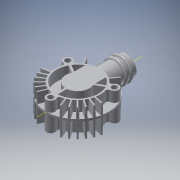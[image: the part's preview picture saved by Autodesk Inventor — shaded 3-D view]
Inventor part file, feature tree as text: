
AUTODESK INVENTOR PART (.ipt)
format: ipt  version: 2016 (Build 200138000, 138)  size: 2,456,576 bytes
history: native  units: in
note: dims shown in document units (in); Inventor stores cm internally (conversion verified against a paired STEP export)
features: sketch x24, extrude x21, pattern_circular x9, plane x4, draft x4, mirror x3, fillet x2, hole x2, revolve x2, other x1, thread x1
ambient origin geometry x8: Origin, YZ Plane, XZ Plane, XY Plane, X Axis, Y Axis, Z Axis, Center Point
bodies: Solid1 (feature_tree)
feature tree (73):
  extrude  "Extrusion1"  Depth=0.05in TaperAngle=0.0deg
  extrude  "Extrusion2"  Depth=1.08in
  extrude  "Extrusion3"  Depth=0.5in
  pattern_circular  "Circular Pattern1"  Count=3 Angle=360.0deg
  plane  "Work Plane2"
  extrude  "Extrusion17"  Depth=0.25in TaperAngle=0.0deg
  extrude  "Extrusion20"  Depth=0.25in
  draft  "FaceDraft5"
  draft  "FaceDraft6"
  fillet  "Fillet6"  Radius=0.125in
  pattern_circular  "Circular Pattern7"  Count=3 Angle=360.0deg
  extrude  "Extrusion21"  Depth=0.25in TaperAngle=360.0deg
  pattern_circular  "Circular Pattern8"  [2 undecoded]
  extrude  "Extrusion22"  Depth=0.25in
  draft  "FaceDraft7"
  draft  "FaceDraft8"
  fillet  "Fillet7"  Radius=0.125in
  pattern_circular  "Circular Pattern9"  [2 undecoded]
  extrude  "Extrusion23"  Depth=0.25in
  pattern_circular  "Circular Pattern10"  [2 undecoded]
  hole  "Hole1"  [1 undecoded]
  pattern_circular  "Circular Pattern11"  [2 undecoded]
  extrude  "Extrusion24"  Depth=0.25in
  plane  "Work Plane5"
  extrude  "Extrusion25"  Depth=0.25in TaperAngle=0.0deg
  hole  "Hole2"  [1 undecoded]
  other  "Work Axis1"
  revolve  "Revolution2"  [1 undecoded]
  pattern_circular  "Circular Pattern2"  [2 undecoded]
  extrude  "Extrusion5"  Depth=0.25in TaperAngle=360.0deg
  extrude  "Extrusion6"  Depth=0.25in
  mirror  "Mirror1"
  mirror  "Mirror2"
  extrude  "Extrusion7"  Depth=0.25in
  extrude  "Extrusion8"  Depth=0.25in TaperAngle=0.0deg
  extrude  "Extrusion9"  Depth=0.25in TaperAngle=360.0deg
  pattern_circular  "Circular Pattern3"  [2 undecoded]
  mirror  "Mirror3"
  extrude  "Extrusion10"  Depth=0.25in
  pattern_circular  "Circular Pattern4"  [2 undecoded]
  extrude  "Extrusion11"  Depth=0.25in
  plane  "Work Plane1"
  extrude  "Extrusion12"  Depth=0.25in TaperAngle=360.0deg
  extrude  "Extrusion13"  Depth=0.25in TaperAngle=0.0deg
  revolve  "Revolution1"  Angle=360.0deg
  extrude  "Extrusion14"  Depth=0.25in
  extrude  "Extrusion16"  Depth=0.25in TaperAngle=360.0deg
  thread  "Thread1"  [1 undecoded]
  sketch  "Sketch1"  dims[d0=1.5in d1=0.05in d2=0.0in]
  sketch  "Sketch2"  dims[d3=1.0in d4=1.08in]
  sketch  "Sketch3"  dims[d5=0.5625in d6=0.5in]
  sketch  "Sketch5"  dims[d7=0.25in d8=0.0in]
  sketch  "Sketch6"  dims[d9=0.05in]
  sketch  "Sketch7"  dims[d10=0.25in d11=0.0in d12=1.1811in d13=360.0deg]
  sketch  "Sketch8"  dims[d20=11.0236in d21=360.0deg d23=0.25in d24=0.0in]
  sketch  "Sketch9"  dims[d25=0.25in d26=0.0in d27=0.5in d28=0.125in d29=0.0in]
  sketch  "Sketch10"  dims[d30=1.0in]
  sketch  "Sketch11"  dims[d31=0.25in d32=0.0in]
  sketch  "Sketch12"  dims[d35=0.25in]
  sketch  "Sketch13"  dims[d36=0.2in]
  sketch  "Sketch14"  dims[d37=0.25in d38=0.0in d39=1.1811in d40=360.0deg]
  sketch  "Sketch15"  dims[d42=0.25in d43=0.0in d44=1.1811in d45=360.0deg]
  sketch  "Sketch17"  dims[d47=0.25in d48=0.0in]
  sketch  "Sketch18"  dims[d49=0.5in]
  sketch  "Sketch20"  dims[d50=0.0625in d51=0.625in d52=0.0in d53=0.0in]
  sketch  "Sketch21"  dims[d54=0.25in d55=0.0in]
  sketch  "Sketch22"  dims[d57=0.1in]
  sketch  "Sketch23"  dims[d58=0.1in]
  sketch  "Sketch24"  dims[d59=0.05in]
  plane  "Work Plane4"
  sketch  "Sketch26"  dims[d60=0.25in]
  sketch  "Sketch27"  dims[d61=0.5in]
  sketch  "Sketch28"  dims[d62=90.0deg d63=0.75in d64=0.0in d67=0.2in d68=0.125in d69=0.0in d70=1.0in d71=0.0in d72=0.25in d76=0.375in d77=0.0in d106=22.5deg d107=0.025in d108=0.025in d109=0.25in d110=0.0in d111=0.0137in d112=0.0137in d113=0.01in d114=12.5984in d115=360.0deg d117=0.1in d118=0.1in d119=0.25in d120=0.0in d121=1.1811in d122=360.0deg d124=0.25in d125=0.0in d126=0.0103in d127=0.0103in d128=0.01in d129=12.5984in d130=360.0deg d132=0.25in d133=0.0in d134=1.1811in d135=360.0deg d137=1.0in d138=1.0in d139=0.129in d140=0.75in d141=0.219in d142=0.112in d143=0.5635in d144=1.0in d145=0.8108in d146=1.1811in d147=360.0deg d149=0.125in d150=0.0in d152=-0.625in d153=0.5in d154=0.5625in d155=0.0in d156=0.313in d157=0.236in d158=0.0246in d159=0.329in d160=0.219in d161=0.112in d162=0.5635in d163=0.25in d164=0.8108in d165=0.125in d166=0.25in d167=90.0deg]
note: 18 required parameter values undecoded (feature->parameter linkage not recoverable at this tier; creation-order binding heuristic only, values carry confidence <= 0.55)